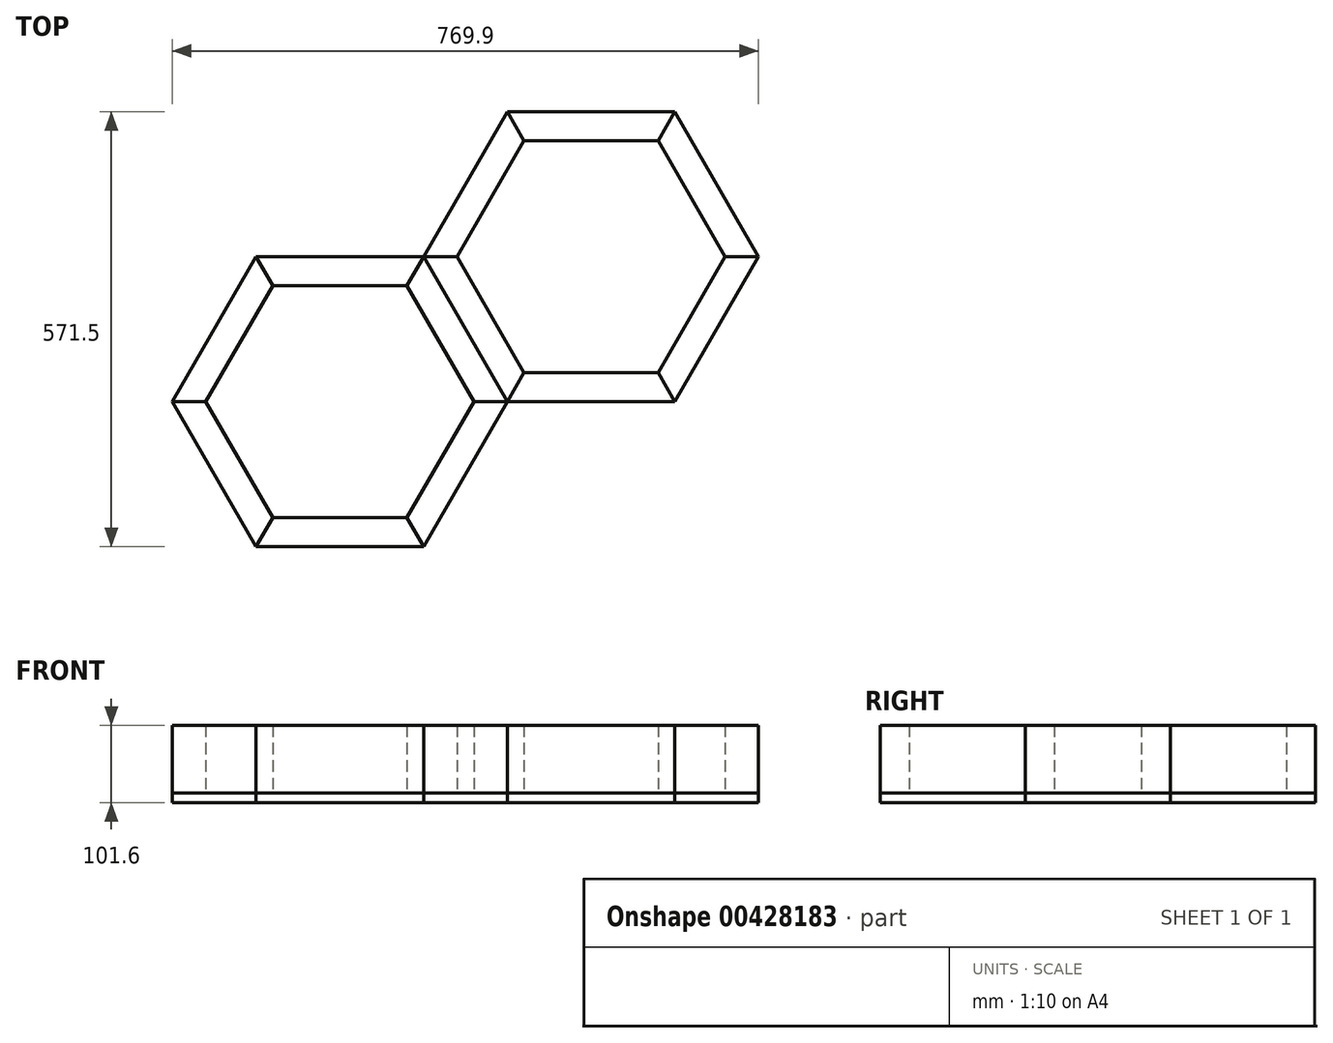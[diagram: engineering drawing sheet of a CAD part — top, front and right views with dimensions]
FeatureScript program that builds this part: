
annotation { "Feature Type Name" : "Feature", "Feature Type Description" : "" }
export const myFeature = defineFeature(function(context is Context, id is Id, definition is map)
    precondition{}
    {
        {
            var Q0;
            Q0=qCreatedBy(makeId("Top.planeOp"),FACE);
            var sketch = newSketch(context, id + "F0", { "sketchPlane" : qUnion([Q0])});
            skCircle(sketch, "E0.cCircle", {"center": v(0, 0) * mm, "radius": 175.98 * mm, "construction": true});
            skLineSegment(sketch, "E0.0", {"start": v(175.98, 0) * mm, "end": v(87.99, -152.4) * mm});
            skLineSegment(sketch, "E0.1", {"start": v(87.99, -152.4) * mm, "end": v(-87.99, -152.4) * mm});
            skLineSegment(sketch, "E0.2", {"start": v(-87.99, -152.4) * mm, "end": v(-175.98, 0) * mm});
            skLineSegment(sketch, "E0.3", {"start": v(-175.98, 0) * mm, "end": v(-87.99, 152.4) * mm});
            skLineSegment(sketch, "E0.4", {"start": v(-87.99, 152.4) * mm, "end": v(87.99, 152.4) * mm});
            skLineSegment(sketch, "E0.5", {"start": v(87.99, 152.4) * mm, "end": v(175.98, 0) * mm});
            skLineSegment(sketch, "E1.0", {"start": v(109.99, 190.5) * mm, "end": v(219.97, 0) * mm});
            skLineSegment(sketch, "E1.1", {"start": v(109.99, -190.5) * mm, "end": v(-109.99, -190.5) * mm});
            skLineSegment(sketch, "E1.2", {"start": v(-109.99, -190.5) * mm, "end": v(-219.97, 0) * mm});
            skLineSegment(sketch, "E1.3", {"start": v(219.97, 0) * mm, "end": v(109.99, -190.5) * mm});
            skLineSegment(sketch, "E1.4", {"start": v(-219.97, 0) * mm, "end": v(-109.99, 190.5) * mm});
            skLineSegment(sketch, "E1.5", {"start": v(-109.99, 190.5) * mm, "end": v(109.99, 190.5) * mm});
            skLineSegment(sketch, "E2", {"start": v(-87.99, 152.4) * mm, "end": v(-109.99, 190.5) * mm});
            skLineSegment(sketch, "E3", {"start": v(87.99, 152.4) * mm, "end": v(109.99, 190.5) * mm});
            skLineSegment(sketch, "E4", {"start": v(175.98, 0) * mm, "end": v(219.97, 0) * mm});
            skLineSegment(sketch, "E5", {"start": v(87.99, -152.4) * mm, "end": v(109.99, -190.5) * mm});
            skLineSegment(sketch, "E6", {"start": v(-87.99, -152.4) * mm, "end": v(-109.99, -190.5) * mm});
            skLineSegment(sketch, "E7", {"start": v(-219.97, 0) * mm, "end": v(-175.98, 0) * mm});
            skSolve(sketch);
        }
        {
            var Q0;
            Q0=makeQuery(id+"F0.imprint","IMPRINT",FACE,{"disambiguationData":[TD([[makeQuery(id+"F0.imprint","IMPRINT",EDGE,{"derivedFrom":sQuery(id+"F0.wireOp",EDGE,"E0.3")}),1.0]])]});
            var Q1;
            Q1=makeQuery(id+"F0.imprint","IMPRINT",FACE,{"disambiguationData":[TD([[makeQuery(id+"F0.imprint","IMPRINT",EDGE,{"derivedFrom":sQuery(id+"F0.wireOp",EDGE,"E0.5")}),1.0]])]});
            var Q2;
            Q2=makeQuery(id+"F0.imprint","IMPRINT",FACE,{"disambiguationData":[TD([[makeQuery(id+"F0.imprint","IMPRINT",EDGE,{"derivedFrom":sQuery(id+"F0.wireOp",EDGE,"E0.1")}),1.0]])]});
            extrude(context, id + "F1", {"entities" : qUnion([Q0, Q1, Q2]), "depth" : 88.9 * mm});
        }
        {
            var Q0;
            Q0=makeQuery(id+"F0.imprint","IMPRINT",FACE,{"disambiguationData":[TD([[makeQuery(id+"F0.imprint","IMPRINT",EDGE,{"derivedFrom":sQuery(id+"F0.wireOp",EDGE,"E0.4")}),1.0]])]});
            var Q1;
            Q1=makeQuery(id+"F0.imprint","IMPRINT",FACE,{"disambiguationData":[TD([[makeQuery(id+"F0.imprint","IMPRINT",EDGE,{"derivedFrom":sQuery(id+"F0.wireOp",EDGE,"E0.2")}),1.0]])]});
            var Q2;
            Q2=makeQuery(id+"F0.imprint","IMPRINT",FACE,{"disambiguationData":[TD([[makeQuery(id+"F0.imprint","IMPRINT",EDGE,{"derivedFrom":sQuery(id+"F0.wireOp",EDGE,"E0.0")}),1.0]])]});
            extrude(context, id + "F2", {"entities" : qUnion([Q0, Q1, Q2]), "depth" : 88.9 * mm});
        }
        {
            var Q0;
            Q0=makeQuery(id+"F0.imprint","IMPRINT",FACE,{"disambiguationData":[TD([[makeQuery(id+"F0.imprint","IMPRINT",EDGE,{"derivedFrom":sQuery(id+"F0.wireOp",EDGE,"E0.2")}),1.0]])]});
            var Q1;
            Q1=makeQuery(id+"F0.imprint","IMPRINT",FACE,{"disambiguationData":[TD([[makeQuery(id+"F0.imprint","IMPRINT",EDGE,{"derivedFrom":sQuery(id+"F0.wireOp",EDGE,"E0.3")}),1.0]])]});
            var Q2;
            Q2=makeQuery(id+"F0.imprint","IMPRINT",FACE,{"disambiguationData":[TD([[makeQuery(id+"F0.imprint","IMPRINT",EDGE,{"derivedFrom":sQuery(id+"F0.wireOp",EDGE,"E0.1")}),1.0]])]});
            var Q3;
            Q3=makeQuery(id+"F0.imprint","IMPRINT",FACE,{"disambiguationData":[TD([[makeQuery(id+"F0.imprint","IMPRINT",EDGE,{"derivedFrom":sQuery(id+"F0.wireOp",EDGE,"E0.4")}),1.0]])]});
            var Q4;
            Q4=makeQuery(id+"F0.imprint","IMPRINT",FACE,{"disambiguationData":[TD([[makeQuery(id+"F0.imprint","IMPRINT",EDGE,{"derivedFrom":sQuery(id+"F0.wireOp",EDGE,"E0.5")}),1.0]])]});
            var Q5;
            Q5=makeQuery(id+"F0.imprint","IMPRINT",FACE,{"disambiguationData":[TD([[makeQuery(id+"F0.imprint","IMPRINT",EDGE,{"derivedFrom":sQuery(id+"F0.wireOp",EDGE,"E0.0")}),-1.0]])]});
            var Q6;
            Q6=makeQuery(id+"F0.imprint","IMPRINT",FACE,{"disambiguationData":[TD([[makeQuery(id+"F0.imprint","IMPRINT",EDGE,{"derivedFrom":sQuery(id+"F0.wireOp",EDGE,"E0.0")}),1.0]])]});
            extrude(context, id + "F3", {"entities" : qUnion([Q0, Q1, Q2, Q3, Q4, Q5, Q6]), "oppositeDirection" : true, "depth" : 12.7 * mm});
        }
        {
            var Q0;
            Q0=makeQuery(id+"F2.opExtrude","SWEPT_BODY",BODY,{"disambiguationData":[OSD([sQuery(id+"F0.wireOp",EDGE,"E0.4"),sQuery(id+"F0.wireOp",EDGE,"E1.5"),sQuery(id+"F0.wireOp",EDGE,"E2"),sQuery(id+"F0.wireOp",EDGE,"E3")])]});
            var Q1;
            Q1=makeQuery(id+"F1.opExtrude","SWEPT_BODY",BODY,{"disambiguationData":[OSD([sQuery(id+"F0.wireOp",EDGE,"E0.5"),sQuery(id+"F0.wireOp",EDGE,"E1.0"),sQuery(id+"F0.wireOp",EDGE,"E3"),sQuery(id+"F0.wireOp",EDGE,"E4")])]});
            var Q2;
            Q2=makeQuery(id+"F2.opExtrude","SWEPT_BODY",BODY,{"disambiguationData":[OSD([sQuery(id+"F0.wireOp",EDGE,"E0.0"),sQuery(id+"F0.wireOp",EDGE,"E1.3"),sQuery(id+"F0.wireOp",EDGE,"E4"),sQuery(id+"F0.wireOp",EDGE,"E5")])]});
            var Q3;
            Q3=makeQuery(id+"F1.opExtrude","SWEPT_BODY",BODY,{"disambiguationData":[OSD([sQuery(id+"F0.wireOp",EDGE,"E0.3"),sQuery(id+"F0.wireOp",EDGE,"E1.4"),sQuery(id+"F0.wireOp",EDGE,"E2"),sQuery(id+"F0.wireOp",EDGE,"E7")])]});
            var Q4;
            Q4=makeQuery(id+"F2.opExtrude","SWEPT_BODY",BODY,{"disambiguationData":[OSD([sQuery(id+"F0.wireOp",EDGE,"E0.2"),sQuery(id+"F0.wireOp",EDGE,"E1.2"),sQuery(id+"F0.wireOp",EDGE,"E6"),sQuery(id+"F0.wireOp",EDGE,"E7")])]});
            var Q5;
            Q5=makeQuery(id+"F3.opExtrude","SWEPT_BODY",BODY,{"disambiguationData":[OSD([sQuery(id+"F0.wireOp",EDGE,"E1.0"),sQuery(id+"F0.wireOp",EDGE,"E1.1"),sQuery(id+"F0.wireOp",EDGE,"E1.2"),sQuery(id+"F0.wireOp",EDGE,"E1.3"),sQuery(id+"F0.wireOp",EDGE,"E1.4"),sQuery(id+"F0.wireOp",EDGE,"E1.5")])]});
            var Q6;
            Q6=makeQuery(id+"F1.opExtrude","SWEPT_BODY",BODY,{"disambiguationData":[OSD([sQuery(id+"F0.wireOp",EDGE,"E0.1"),sQuery(id+"F0.wireOp",EDGE,"E1.1"),sQuery(id+"F0.wireOp",EDGE,"E5"),sQuery(id+"F0.wireOp",EDGE,"E6")])]});
            var Q7;
            Q7=makeQuery(id+"F2.opExtrude","SWEPT_FACE",FACE,{"disambiguationData":[OSD([sQuery(id+"F0.wireOp",EDGE,"E1.2")])]});
            mirror(context, id + "F4", {"entities" : qUnion([Q0, Q1, Q2, Q3, Q4, Q5, Q6]), "mirrorPlane" : qUnion([Q7])});
        }
    });
